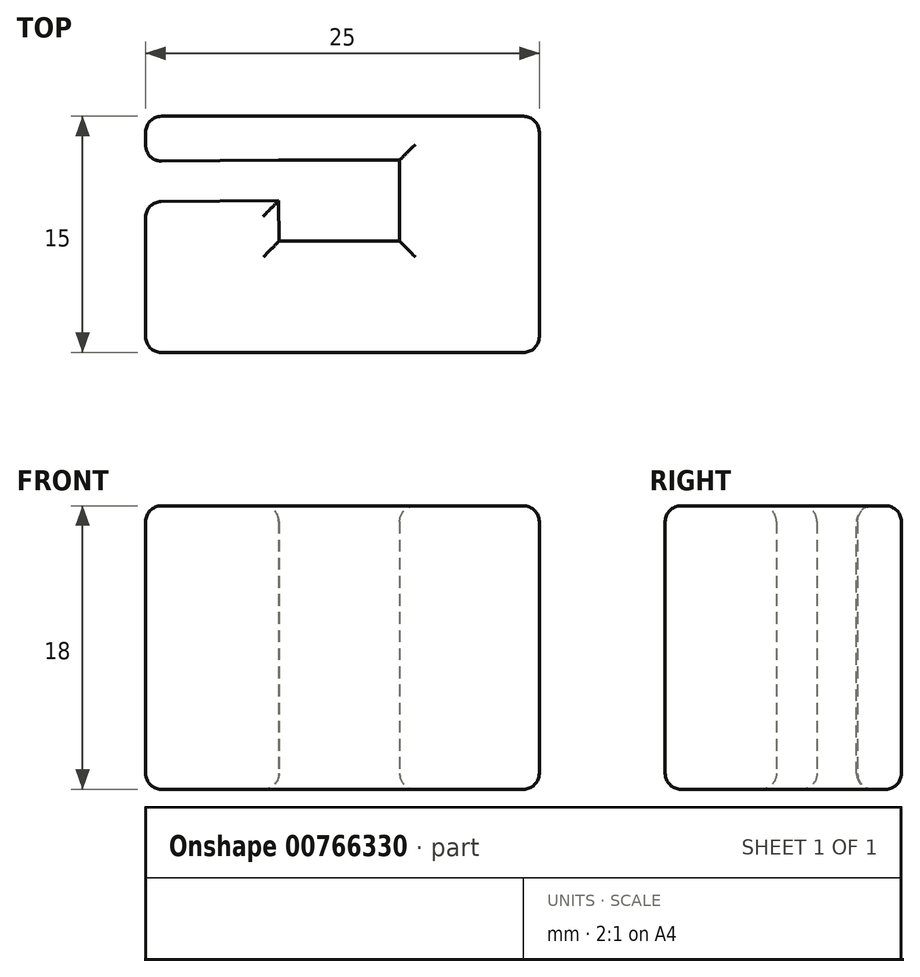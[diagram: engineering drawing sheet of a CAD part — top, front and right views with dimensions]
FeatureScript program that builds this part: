
annotation { "Feature Type Name" : "Feature", "Feature Type Description" : "" }
export const myFeature = defineFeature(function(context is Context, id is Id, definition is map)
    precondition{}
    {
        {
            var Q0;
            Q0=qCreatedBy(makeId("Top.planeOp"),FACE);
            var sketch = newSketch(context, id + "F0", { "sketchPlane" : qUnion([Q0])});
            skLineSegment(sketch, "E0", {"start": v(-6.57, 5.21) * mm, "end": v(1.13, 5.21) * mm});
            skLineSegment(sketch, "E1", {"start": v(1.13, 5.21) * mm, "end": v(1.13, 0.06) * mm});
            skLineSegment(sketch, "E2", {"start": v(1.13, 0.06) * mm, "end": v(-6.53, 0.06) * mm});
            skLineSegment(sketch, "E3", {"start": v(-15, 8) * mm, "end": v(10, 8) * mm});
            skLineSegment(sketch, "E4", {"start": v(10, 8) * mm, "end": v(10, -7) * mm});
            skLineSegment(sketch, "E5", {"start": v(10, -7) * mm, "end": v(-15, -7) * mm});
            skLineSegment(sketch, "E6", {"start": v(-6.57, 5.21) * mm, "end": v(-15, 5.14) * mm});
            skLineSegment(sketch, "E7", {"start": v(-6.55, 2.64) * mm, "end": v(-15, 2.57) * mm});
            skLineSegment(sketch, "E8", {"start": v(-15, -7) * mm, "end": v(-15, 2.57) * mm});
            skLineSegment(sketch, "E9", {"start": v(-15, 8) * mm, "end": v(-15, 5.14) * mm});
            skLineSegment(sketch, "E10", {"start": v(-6.55, 2.64) * mm, "end": v(-6.53, 0.06) * mm});
            skSolve(sketch);
        }
        {
            var Q0;
            Q0=makeQuery(id+"F0.imprint","IMPRINT",FACE,{"disambiguationData":[TD([[makeQuery(id+"F0.imprint","IMPRINT",EDGE,{"derivedFrom":sQuery(id+"F0.wireOp",EDGE,"E0")}),1.0]])]});
            extrude(context, id + "F1", {"entities" : qUnion([Q0]), "depth" : 18 * mm, "offsetDistance" : 25 * mm});
        }
        {
            var Q0;
            Q0=makeQuery(id+"F1.opExtrude","CAP_EDGE",EDGE,{"disambiguationData":[OSD([sQuery(id+"F0.wireOp",EDGE,"E5")])],"isStart":false});
            var Q1;
            Q1=makeQuery(id+"F1.opExtrude","CAP_EDGE",EDGE,{"disambiguationData":[OSD([sQuery(id+"F0.wireOp",EDGE,"E2")])],"isStart":false});
            var Q2;
            Q2=makeQuery(id+"F1.opExtrude","CAP_EDGE",EDGE,{"disambiguationData":[OSD([sQuery(id+"F0.wireOp",EDGE,"E0")])],"isStart":false});
            var Q3;
            Q3=makeQuery(id+"F1.opExtrude","CAP_EDGE",EDGE,{"disambiguationData":[OSD([sQuery(id+"F0.wireOp",EDGE,"E6")])],"isStart":false});
            var Q4;
            Q4=makeQuery(id+"F1.opExtrude","CAP_EDGE",EDGE,{"disambiguationData":[OSD([sQuery(id+"F0.wireOp",EDGE,"E1")])],"isStart":false});
            var Q5;
            Q5=makeQuery(id+"F1.opExtrude","CAP_EDGE",EDGE,{"disambiguationData":[OSD([sQuery(id+"F0.wireOp",EDGE,"E10")])],"isStart":false});
            var Q6;
            Q6=makeQuery(id+"F1.opExtrude","CAP_EDGE",EDGE,{"disambiguationData":[OSD([sQuery(id+"F0.wireOp",EDGE,"E7")])],"isStart":false});
            var Q7;
            Q7=makeQuery(id+"F1.opExtrude","CAP_EDGE",EDGE,{"disambiguationData":[OSD([sQuery(id+"F0.wireOp",EDGE,"E9")])],"isStart":false});
            var Q8;
            Q8=makeQuery(id+"F1.opExtrude","CAP_EDGE",EDGE,{"disambiguationData":[OSD([sQuery(id+"F0.wireOp",EDGE,"E3")])],"isStart":false});
            var Q9;
            Q9=makeQuery(id+"F1.opExtrude","CAP_EDGE",EDGE,{"disambiguationData":[OSD([sQuery(id+"F0.wireOp",EDGE,"E8")])],"isStart":false});
            var Q10;
            Q10=makeQuery(id+"F1.opExtrude","SWEPT_EDGE",EDGE,{"disambiguationData":[OSD([sQuery(id+"F0.wireOp",EDGE,"E7"),sQuery(id+"F0.wireOp",EDGE,"E8")])]});
            var Q11;
            Q11=makeQuery(id+"F1.opExtrude","SWEPT_EDGE",EDGE,{"disambiguationData":[OSD([sQuery(id+"F0.wireOp",EDGE,"E6"),sQuery(id+"F0.wireOp",EDGE,"E9")])]});
            var Q12;
            Q12=makeQuery(id+"F1.opExtrude","SWEPT_EDGE",EDGE,{"disambiguationData":[OSD([sQuery(id+"F0.wireOp",EDGE,"E5"),sQuery(id+"F0.wireOp",EDGE,"E8")])]});
            var Q13;
            Q13=makeQuery(id+"F1.opExtrude","CAP_EDGE",EDGE,{"disambiguationData":[OSD([sQuery(id+"F0.wireOp",EDGE,"E8")])],"isStart":true});
            var Q14;
            Q14=makeQuery(id+"F1.opExtrude","CAP_EDGE",EDGE,{"disambiguationData":[OSD([sQuery(id+"F0.wireOp",EDGE,"E7")])],"isStart":true});
            var Q15;
            Q15=makeQuery(id+"F1.opExtrude","CAP_EDGE",EDGE,{"disambiguationData":[OSD([sQuery(id+"F0.wireOp",EDGE,"E10")])],"isStart":true});
            var Q16;
            Q16=makeQuery(id+"F1.opExtrude","CAP_EDGE",EDGE,{"disambiguationData":[OSD([sQuery(id+"F0.wireOp",EDGE,"E2")])],"isStart":true});
            var Q17;
            Q17=makeQuery(id+"F1.opExtrude","CAP_EDGE",EDGE,{"disambiguationData":[OSD([sQuery(id+"F0.wireOp",EDGE,"E1")])],"isStart":true});
            var Q18;
            Q18=makeQuery(id+"F1.opExtrude","CAP_EDGE",EDGE,{"disambiguationData":[OSD([sQuery(id+"F0.wireOp",EDGE,"E0")])],"isStart":true});
            var Q19;
            Q19=makeQuery(id+"F1.opExtrude","CAP_EDGE",EDGE,{"disambiguationData":[OSD([sQuery(id+"F0.wireOp",EDGE,"E9")])],"isStart":true});
            var Q20;
            Q20=makeQuery(id+"F1.opExtrude","CAP_EDGE",EDGE,{"disambiguationData":[OSD([sQuery(id+"F0.wireOp",EDGE,"E3")])],"isStart":true});
            var Q21;
            Q21=makeQuery(id+"F1.opExtrude","SWEPT_EDGE",EDGE,{"disambiguationData":[OSD([sQuery(id+"F0.wireOp",EDGE,"E3"),sQuery(id+"F0.wireOp",EDGE,"E9")])]});
            var Q22;
            Q22=makeQuery(id+"F1.opExtrude","CAP_EDGE",EDGE,{"disambiguationData":[OSD([sQuery(id+"F0.wireOp",EDGE,"E4")])],"isStart":true});
            var Q23;
            Q23=makeQuery(id+"F1.opExtrude","CAP_EDGE",EDGE,{"disambiguationData":[OSD([sQuery(id+"F0.wireOp",EDGE,"E5")])],"isStart":true});
            var Q24;
            Q24=makeQuery(id+"F1.opExtrude","SWEPT_EDGE",EDGE,{"disambiguationData":[OSD([sQuery(id+"F0.wireOp",EDGE,"E4"),sQuery(id+"F0.wireOp",EDGE,"E5")])]});
            var Q25;
            Q25=makeQuery(id+"F1.opExtrude","SWEPT_EDGE",EDGE,{"disambiguationData":[OSD([sQuery(id+"F0.wireOp",EDGE,"E3"),sQuery(id+"F0.wireOp",EDGE,"E4")])]});
            var Q26;
            Q26=makeQuery(id+"F1.opExtrude","CAP_EDGE",EDGE,{"disambiguationData":[OSD([sQuery(id+"F0.wireOp",EDGE,"E4")])],"isStart":false});
            fillet(context, id + "F2", {"entities" : qUnion([Q0, Q1, Q2, Q3, Q4, Q5, Q6, Q7, Q8, Q9, Q10, Q11, Q12, Q13, Q14, Q15, Q16, Q17, Q18, Q19, Q20, Q21, Q22, Q23, Q24, Q25, Q26]), "radius" : 1 * mm, "tangentPropagation" : true, "allowEdgeOverflow" : false});
        }
    });
